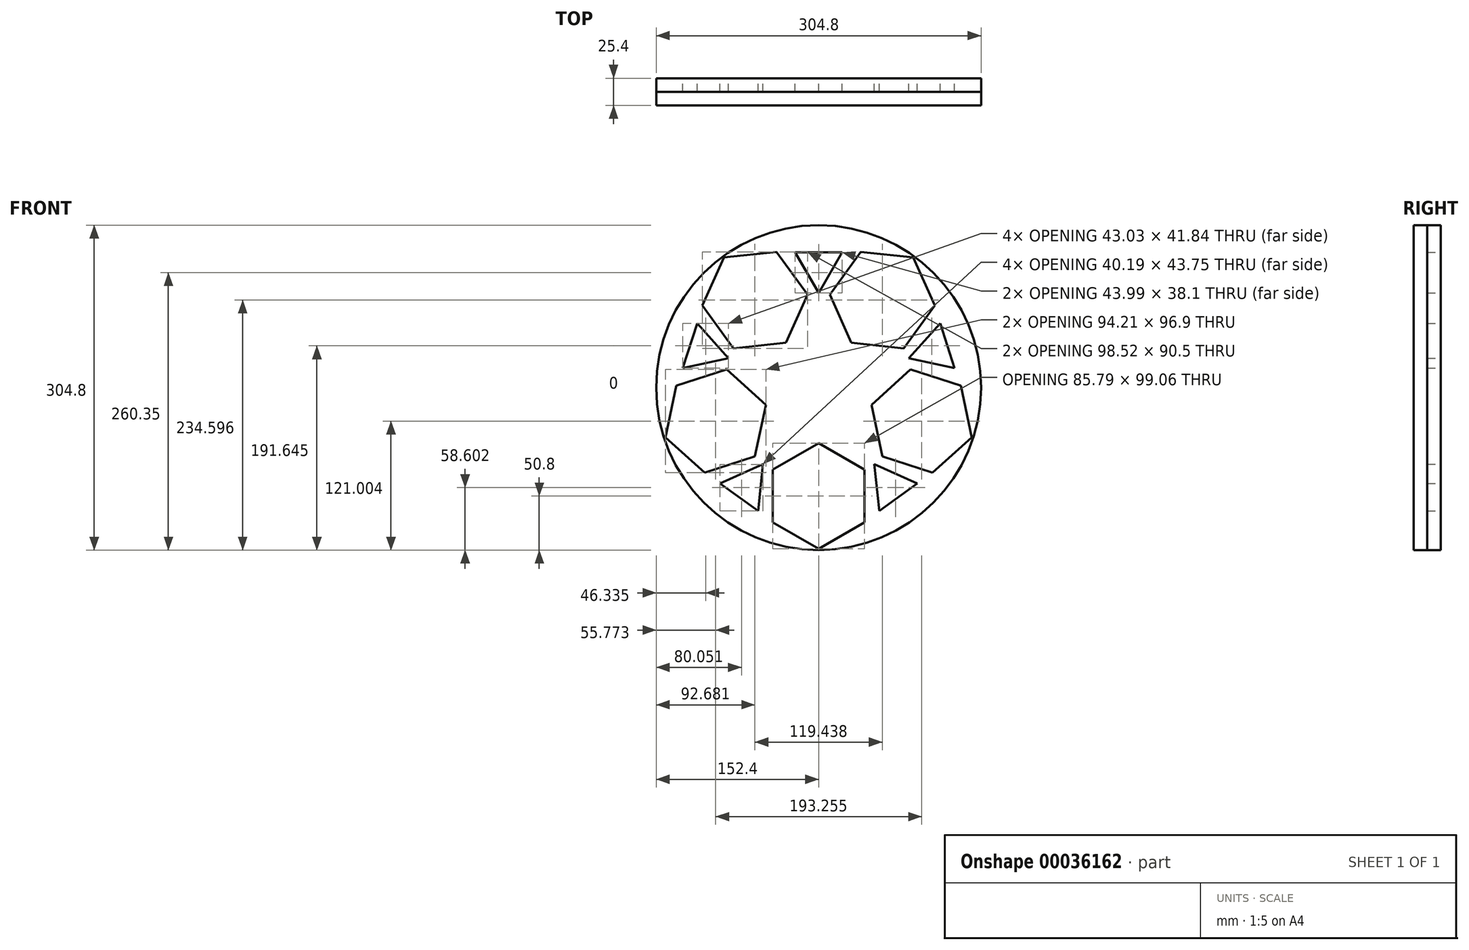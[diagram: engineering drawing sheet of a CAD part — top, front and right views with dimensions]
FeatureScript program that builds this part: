
annotation { "Feature Type Name" : "Feature", "Feature Type Description" : "" }
export const myFeature = defineFeature(function(context is Context, id is Id, definition is map)
    precondition{}
    {
        {
            var Q0;
            Q0=qCreatedBy(makeId("Front.planeOp"),FACE);
            var sketch = newSketch(context, id + "F0", { "sketchPlane" : qUnion([Q0])});
            skCircle(sketch, "E0", {"center": v(0, 0) * mm, "radius": 152.4 * mm});
            skCircle(sketch, "E1", {"center": v(0, 0) * mm, "radius": 101.6 * mm, "construction": true});
            skLineSegment(sketch, "E2", {"start": v(0, 0) * mm, "end": v(0, -101.6) * mm, "construction": true});
            skCircle(sketch, "E3.cCircle", {"center": v(0, -101.6) * mm, "radius": 49.53 * mm, "construction": true});
            skLineSegment(sketch, "E3.0", {"start": v(42.9, -126.36) * mm, "end": v(0, -151.13) * mm});
            skLineSegment(sketch, "E3.1", {"start": v(0, -151.13) * mm, "end": v(-42.9, -126.37) * mm});
            skLineSegment(sketch, "E3.2", {"start": v(-42.9, -126.36) * mm, "end": v(-42.9, -76.83) * mm});
            skLineSegment(sketch, "E3.3", {"start": v(-42.9, -76.84) * mm, "end": v(0, -52.07) * mm});
            skLineSegment(sketch, "E3.4", {"start": v(0, -52.07) * mm, "end": v(42.9, -76.84) * mm});
            skLineSegment(sketch, "E3.5", {"start": v(42.9, -76.84) * mm, "end": v(42.9, -126.37) * mm});
            skLineSegment(sketch, "E4.1.0", {"start": v(133.44, 1.75) * mm, "end": v(143.73, -46.7) * mm});
            skLineSegment(sketch, "E4.1.1", {"start": v(143.73, -46.7) * mm, "end": v(106.93, -79.84) * mm});
            skLineSegment(sketch, "E4.1.2", {"start": v(106.93, -79.84) * mm, "end": v(59.82, -64.54) * mm});
            skLineSegment(sketch, "E4.1.3", {"start": v(59.82, -64.54) * mm, "end": v(49.52, -16.1) * mm});
            skLineSegment(sketch, "E4.1.4", {"start": v(49.52, -16.1) * mm, "end": v(86.33, 17.05) * mm});
            skLineSegment(sketch, "E4.1.5", {"start": v(86.33, 17.05) * mm, "end": v(133.44, 1.75) * mm});
            skLineSegment(sketch, "E4.2.0", {"start": v(39.57, 127.44) * mm, "end": v(88.83, 122.27) * mm});
            skLineSegment(sketch, "E4.2.1", {"start": v(88.83, 122.27) * mm, "end": v(108.98, 77.02) * mm});
            skLineSegment(sketch, "E4.2.2", {"start": v(108.98, 77.02) * mm, "end": v(79.86, 36.95) * mm});
            skLineSegment(sketch, "E4.2.3", {"start": v(79.86, 36.95) * mm, "end": v(30.6, 42.13) * mm});
            skLineSegment(sketch, "E4.2.4", {"start": v(30.6, 42.13) * mm, "end": v(10.46, 87.37) * mm});
            skLineSegment(sketch, "E4.2.5", {"start": v(10.46, 87.37) * mm, "end": v(39.57, 127.44) * mm});
            skLineSegment(sketch, "E4.3.0", {"start": v(-108.98, 77.02) * mm, "end": v(-88.83, 122.27) * mm});
            skLineSegment(sketch, "E4.3.1", {"start": v(-88.83, 122.27) * mm, "end": v(-39.57, 127.44) * mm});
            skLineSegment(sketch, "E4.3.2", {"start": v(-39.57, 127.44) * mm, "end": v(-10.46, 87.37) * mm});
            skLineSegment(sketch, "E4.3.3", {"start": v(-10.46, 87.37) * mm, "end": v(-30.6, 42.13) * mm});
            skLineSegment(sketch, "E4.3.4", {"start": v(-30.6, 42.13) * mm, "end": v(-79.86, 36.95) * mm});
            skLineSegment(sketch, "E4.3.5", {"start": v(-79.86, 36.95) * mm, "end": v(-108.98, 77.02) * mm});
            skLineSegment(sketch, "E4.4.0", {"start": v(-106.93, -79.84) * mm, "end": v(-143.73, -46.7) * mm});
            skLineSegment(sketch, "E4.4.1", {"start": v(-143.73, -46.7) * mm, "end": v(-133.44, 1.75) * mm});
            skLineSegment(sketch, "E4.4.2", {"start": v(-133.44, 1.75) * mm, "end": v(-86.33, 17.05) * mm});
            skLineSegment(sketch, "E4.4.3", {"start": v(-86.33, 17.05) * mm, "end": v(-49.52, -16.1) * mm});
            skLineSegment(sketch, "E4.4.4", {"start": v(-49.52, -16.1) * mm, "end": v(-59.82, -64.54) * mm});
            skLineSegment(sketch, "E4.4.5", {"start": v(-59.82, -64.54) * mm, "end": v(-106.93, -79.84) * mm});
            skCircle(sketch, "E5", {"center": v(0, 0) * mm, "radius": 114.3 * mm, "construction": true});
            skLineSegment(sketch, "E6", {"start": v(0, 0) * mm, "end": v(0, 114.3) * mm, "construction": true});
            skCircle(sketch, "E7.cCircle", {"center": v(0, 114.3) * mm, "radius": 25.4 * mm, "construction": true});
            skLineSegment(sketch, "E7.0", {"start": v(0, 88.9) * mm, "end": v(-22, 127) * mm});
            skLineSegment(sketch, "E7.1", {"start": v(-22, 127) * mm, "end": v(22, 127) * mm});
            skLineSegment(sketch, "E7.2", {"start": v(22, 127) * mm, "end": v(0, 88.9) * mm});
            skLineSegment(sketch, "E8.1.0", {"start": v(-127.58, 18.32) * mm, "end": v(-113.99, 60.17) * mm});
            skLineSegment(sketch, "E8.1.1", {"start": v(-84.55, 27.47) * mm, "end": v(-127.58, 18.32) * mm});
            skLineSegment(sketch, "E8.1.2", {"start": v(-113.99, 60.17) * mm, "end": v(-84.55, 27.47) * mm});
            skLineSegment(sketch, "E8.2.0", {"start": v(-56.85, -115.67) * mm, "end": v(-92.44, -89.82) * mm});
            skLineSegment(sketch, "E8.2.1", {"start": v(-52.25, -71.92) * mm, "end": v(-56.85, -115.67) * mm});
            skLineSegment(sketch, "E8.2.2", {"start": v(-92.44, -89.82) * mm, "end": v(-52.25, -71.92) * mm});
            skLineSegment(sketch, "E8.3.0", {"start": v(92.44, -89.82) * mm, "end": v(56.85, -115.67) * mm});
            skLineSegment(sketch, "E8.3.1", {"start": v(52.25, -71.92) * mm, "end": v(92.44, -89.82) * mm});
            skLineSegment(sketch, "E8.3.2", {"start": v(56.85, -115.67) * mm, "end": v(52.25, -71.92) * mm});
            skLineSegment(sketch, "E8.4.0", {"start": v(113.99, 60.17) * mm, "end": v(127.58, 18.32) * mm});
            skLineSegment(sketch, "E8.4.1", {"start": v(84.55, 27.47) * mm, "end": v(113.99, 60.17) * mm});
            skLineSegment(sketch, "E8.4.2", {"start": v(127.58, 18.32) * mm, "end": v(84.55, 27.47) * mm});
            skSolve(sketch);
        }
        {
            var Q0;
            Q0=makeQuery(id+"F0.imprint","IMPRINT",FACE,{"disambiguationData":[TD([[makeQuery(id+"F0.imprint","IMPRINT",EDGE,{"derivedFrom":sQuery(id+"F0.wireOp",EDGE,"E0")}),1.0]])]});
            extrude(context, id + "F2", {"entities" : qUnion([Q0]), "depth" : 25.4 * mm});
        }
        {
            var Q0;
            Q0=makeQuery(id+"F0.imprint","IMPRINT",FACE,{"disambiguationData":[TD([[makeQuery(id+"F0.imprint","IMPRINT",EDGE,{"derivedFrom":sQuery(id+"F0.wireOp",EDGE,"E4.3.0")}),-1.0]])]});
            var Q1;
            Q1=makeQuery(id+"F0.imprint","IMPRINT",FACE,{"disambiguationData":[TD([[makeQuery(id+"F0.imprint","IMPRINT",EDGE,{"derivedFrom":sQuery(id+"F0.wireOp",EDGE,"E4.4.0")}),-1.0]])]});
            var Q2;
            Q2=makeQuery(id+"F0.imprint","IMPRINT",FACE,{"disambiguationData":[TD([[makeQuery(id+"F0.imprint","IMPRINT",EDGE,{"derivedFrom":sQuery(id+"F0.wireOp",EDGE,"E3.0")}),-1.0]])]});
            var Q3;
            {var subQ0=sQuery(id+"F0.wireOp",EDGE,"E3.0");Q3=makeQuery(id+"F0.imprint","IMPRINT",FACE,{"disambiguationData":[TD([[makeQuery(id+"F0.imprint","IMPRINT",EDGE,{"derivedFrom":subQ0}),1.0]])]});}
            var Q4;
            Q4=makeQuery(id+"F0.imprint","IMPRINT",FACE,{"disambiguationData":[TD([[makeQuery(id+"F0.imprint","IMPRINT",EDGE,{"derivedFrom":sQuery(id+"F0.wireOp",EDGE,"E4.1.0")}),-1.0]])]});
            var Q5;
            Q5=makeQuery(id+"F0.imprint","IMPRINT",FACE,{"disambiguationData":[TD([[makeQuery(id+"F0.imprint","IMPRINT",EDGE,{"derivedFrom":sQuery(id+"F0.wireOp",EDGE,"E4.2.0")}),-1.0]])]});
            extrude(context, id + "F1", {"entities" : qUnion([Q0, Q1, Q2, Q3, Q4, Q5]), "depth" : 12.7 * mm});
        }
    });
